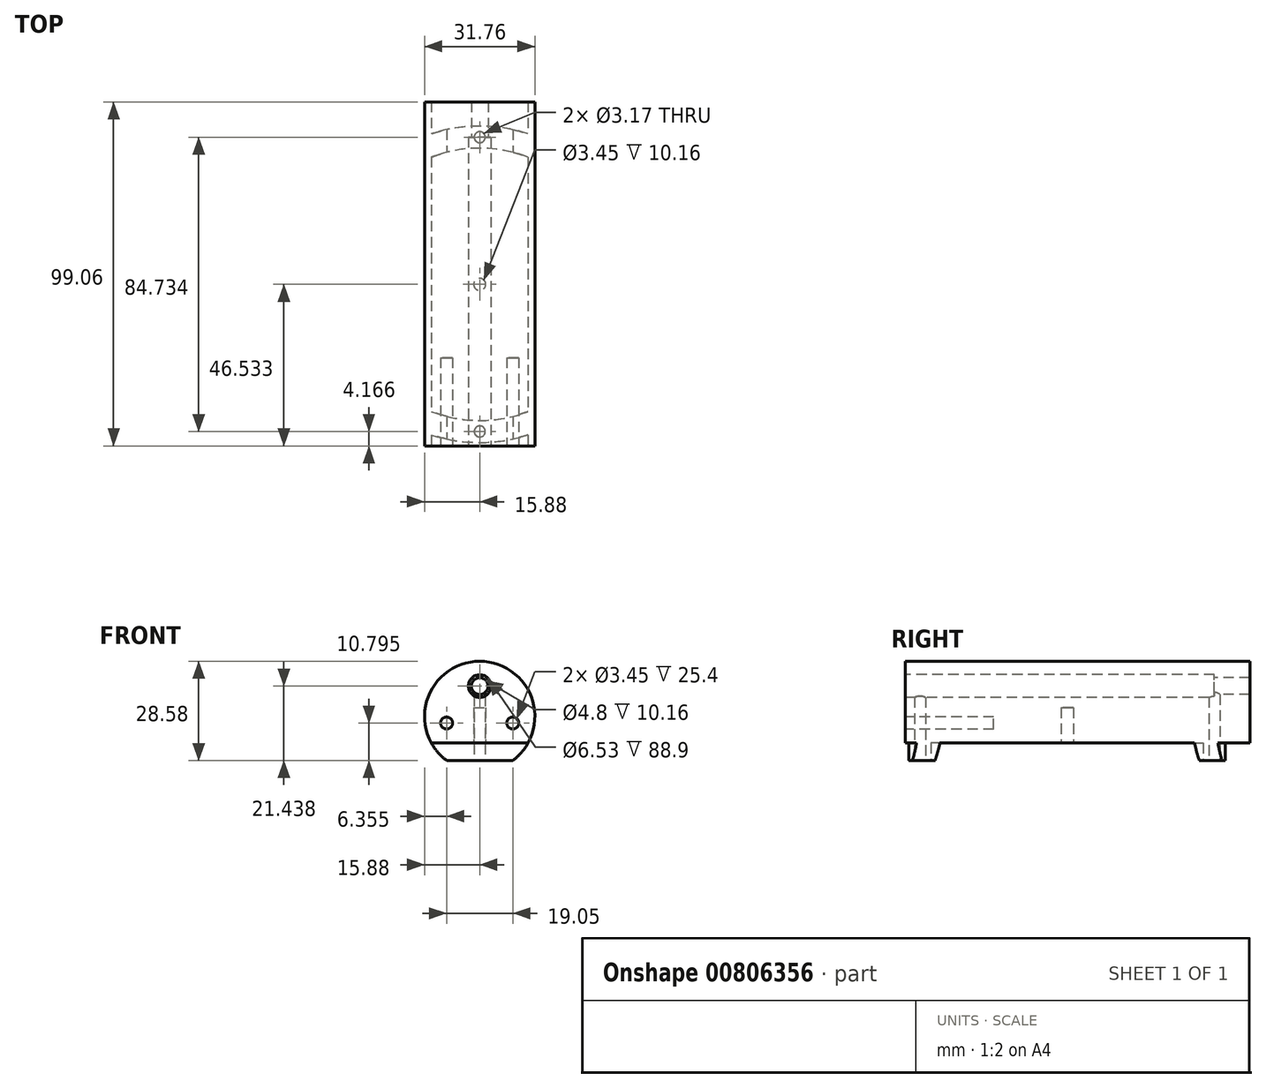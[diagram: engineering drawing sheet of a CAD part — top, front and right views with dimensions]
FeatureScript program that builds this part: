
annotation { "Feature Type Name" : "Feature", "Feature Type Description" : "" }
export const myFeature = defineFeature(function(context is Context, id is Id, definition is map)
    precondition{}
    {
        {
            var Q0;
            Q0=qCreatedBy(makeId("Front.planeOp"),FACE);
            var sketch = newSketch(context, id + "F0", { "sketchPlane" : qUnion([Q0])});
            skArc(sketch, "E0", {"start": v(9.52, -12.7) * mm, "mid": v(0, 15.88) * mm, "end": v(-9.53, -12.7) * mm});
            skLineSegment(sketch, "E1", {"start": v(-9.52, -12.7) * mm, "end": v(9.52, -12.7) * mm});
            skCircle(sketch, "E2", {"center": v(0, 8.74) * mm, "radius": 3.26 * mm});
            skLineSegment(sketch, "E3", {"start": v(-13.38, -1.9) * mm, "end": v(6.88, -1.9) * mm, "construction": true});
            skCircle(sketch, "E4", {"center": v(-9.52, -1.9) * mm, "radius": 1.73 * mm});
            skCircle(sketch, "E5", {"center": v(9.53, -1.9) * mm, "radius": 1.73 * mm});
            skCircle(sketch, "E6", {"center": v(0, 8.74) * mm, "radius": 2.4 * mm});
            skSolve(sketch);
        }
        {
            var Q0;
            Q0 = qSketchRegion(id + "F0", true);
            var Q1;
            Q1=makeQuery(id+"F0.imprint","IMPRINT",FACE,{"disambiguationData":[TD([[makeQuery(id+"F0.imprint","IMPRINT",EDGE,{"derivedFrom":sQuery(id+"F0.wireOp",EDGE,"E2")}),1.0]])]});
            var Q2;
            Q2=makeQuery(id+"F0.imprint","IMPRINT",FACE,{"disambiguationData":[TD([[makeQuery(id+"F0.imprint","IMPRINT",EDGE,{"derivedFrom":sQuery(id+"F0.wireOp",EDGE,"E4")}),1.0]])]});
            var Q3;
            Q3=makeQuery(id+"F0.imprint","IMPRINT",FACE,{"disambiguationData":[TD([[makeQuery(id+"F0.imprint","IMPRINT",EDGE,{"derivedFrom":sQuery(id+"F0.wireOp",EDGE,"E5")}),1.0]])]});
            extrude(context, id + "F1", {"entities" : qUnion([Q0, Q1, Q2, Q3]), "oppositeDirection" : true, "depth" : 99.06 * mm, "offsetDistance" : 25.4 * mm});
        }
        {
            var Q0;
            Q0=makeQuery(id+"F0.imprint","IMPRINT",FACE,{"disambiguationData":[TD([[makeQuery(id+"F0.imprint","IMPRINT",EDGE,{"derivedFrom":sQuery(id+"F0.wireOp",EDGE,"E2")}),1.0]])]});
            extrude(context, id + "F2", {"entities" : qUnion([Q0]), "operationType" : NewBodyOperationType.REMOVE, "endBound" : BoundingType.UP_TO_NEXT, "oppositeDirection" : true, "depth" : 25.4 * mm, "hasOffset" : true, "offsetDistance" : 10.16 * mm});
        }
        {
            var Q0;
            Q0=makeQuery(id+"F0.imprint","IMPRINT",FACE,{"disambiguationData":[TD([[makeQuery(id+"F0.imprint","IMPRINT",EDGE,{"derivedFrom":sQuery(id+"F0.wireOp",EDGE,"E4")}),1.0]])]});
            var Q1;
            Q1=makeQuery(id+"F0.imprint","IMPRINT",FACE,{"disambiguationData":[TD([[makeQuery(id+"F0.imprint","IMPRINT",EDGE,{"derivedFrom":sQuery(id+"F0.wireOp",EDGE,"E5")}),1.0]])]});
            extrude(context, id + "F3", {"entities" : qUnion([Q0, Q1]), "operationType" : NewBodyOperationType.REMOVE, "oppositeDirection" : true, "depth" : 25.4 * mm, "offsetDistance" : 25.4 * mm});
        }
        {
            var Q0;
            Q0=makeQuery(id+"F0.imprint","IMPRINT",FACE,{"disambiguationData":[TD([[makeQuery(id+"F0.imprint","IMPRINT",EDGE,{"derivedFrom":sQuery(id+"F0.wireOp",EDGE,"E6")}),1.0]])]});
            extrude(context, id + "F4", {"entities" : qUnion([Q0]), "operationType" : NewBodyOperationType.REMOVE, "endBound" : BoundingType.THROUGH_ALL, "oppositeDirection" : true, "depth" : 25.4 * mm, "offsetDistance" : 25.4 * mm});
        }
        {
            var Q0;
            Q0=makeQuery(id+"F1.opExtrude","SWEPT_FACE",FACE,{"disambiguationData":[OSD([sQuery(id+"F0.wireOp",EDGE,"E1")])]});
            var sketch = newSketch(context, id + "F5", { "sketchPlane" : qUnion([Q0])});
            skCircle(sketch, "E7", {"center": v(0, -46.53) * mm, "radius": 1.73 * mm});
            skCircle(sketch, "E8", {"center": v(0, -88.9) * mm, "radius": 1.59 * mm});
            skCircle(sketch, "E9", {"center": v(0, -4.17) * mm, "radius": 1.59 * mm});
            skArc(sketch, "E10.trimOffspring", {"start": v(9.53, -8.52) * mm, "mid": v(0, -7.34) * mm, "end": v(-9.53, -8.52) * mm});
            skArc(sketch, "E11.trimOffspring", {"start": v(9.52, -2) * mm, "mid": v(0, -1) * mm, "end": v(-9.53, -2) * mm});
            skLineSegment(sketch, "E12.bottom", {"start": v(-9.53, -99.06) * mm, "end": v(9.52, -99.06) * mm});
            skLineSegment(sketch, "E12.top", {"start": v(-9.53, 0) * mm, "end": v(9.52, 0) * mm});
            skLineSegment(sketch, "E13.bottom", {"start": v(9.52, -99.06) * mm, "end": v(19.26, -99.06) * mm});
            skLineSegment(sketch, "E13.top", {"start": v(9.52, 0) * mm, "end": v(19.26, 0) * mm});
            skLineSegment(sketch, "E13.right", {"start": v(19.26, -99.06) * mm, "end": v(19.26, 0) * mm});
            skLineSegment(sketch, "E14.bottom", {"start": v(-9.53, 0) * mm, "end": v(-24.1, 0) * mm});
            skLineSegment(sketch, "E14.top", {"start": v(-9.53, -99.06) * mm, "end": v(-24.1, -99.06) * mm});
            skLineSegment(sketch, "E14.right", {"start": v(-24.1, 0) * mm, "end": v(-24.1, -99.06) * mm});
            skArc(sketch, "E15.converted", {"start": v(19.26, -5.26) * mm, "mid": v(-2.76, -1.07) * mm, "end": v(-24.1, -7.9) * mm});
            skArc(sketch, "E16.converted", {"start": v(19.26, -12.4) * mm, "mid": v(-2.91, -7.45) * mm, "end": v(-24.1, -15.63) * mm});
            skArc(sketch, "E17.trimOffspring", {"start": v(-24.1, -77.43) * mm, "mid": v(-2.91, -85.62) * mm, "end": v(19.26, -80.67) * mm});
            skArc(sketch, "E18.trimOffspring", {"start": v(-24.1, -85.17) * mm, "mid": v(-2.76, -92) * mm, "end": v(19.26, -87.8) * mm});
            skSolve(sketch);
        }
        {
            var Q0;
            {var subQ0=sQuery(id+"F5.wireOp",EDGE,"E16.converted");var subQ1=sQuery(id+"F5.wireOp",EDGE,"E14.right");var subQ2=makeQuery(id+"F5.imprint","INTERSECT",VERTEX,{"derivedFrom":[subQ1,subQ0]});Q0=makeQuery(id+"F5.imprint","IMPRINT",FACE,{"disambiguationData":[TD([[makeQuery(id+"F5.imprint","IMPRINT",EDGE,{"disambiguationData":[TD([[subQ2,-1.0]])],"derivedFrom":subQ1}),1.0]])]});}
            var Q1;
            Q1=makeQuery(id+"F5.imprint","IMPRINT",FACE,{"disambiguationData":[TD([[makeQuery(id+"F5.imprint","IMPRINT",EDGE,{"derivedFrom":sQuery(id+"F5.wireOp",EDGE,"E7")}),-1.0]])]});
            var Q2;
            {var subQ0=sQuery(id+"F5.wireOp",EDGE,"E16.converted");var subQ1=sQuery(id+"F5.wireOp",EDGE,"E13.right");var subQ2=makeQuery(id+"F5.imprint","INTERSECT",VERTEX,{"derivedFrom":[subQ1,subQ0]});Q2=makeQuery(id+"F5.imprint","IMPRINT",FACE,{"disambiguationData":[TD([[makeQuery(id+"F5.imprint","IMPRINT",EDGE,{"disambiguationData":[TD([[subQ2,1.0]])],"derivedFrom":subQ1}),1.0]])]});}
            var Q3;
            {var subQ0=sQuery(id+"F5.wireOp",EDGE,"E13.bottom");Q3=makeQuery(id+"F5.imprint","IMPRINT",FACE,{"disambiguationData":[TD([[makeQuery(id+"F5.imprint","IMPRINT",EDGE,{"derivedFrom":subQ0}),1.0]])]});}
            var Q4;
            {var subQ0=sQuery(id+"F5.wireOp",EDGE,"E12.bottom");Q4=makeQuery(id+"F5.imprint","IMPRINT",FACE,{"disambiguationData":[TD([[makeQuery(id+"F5.imprint","IMPRINT",EDGE,{"derivedFrom":subQ0}),1.0]])]});}
            var Q5;
            {var subQ0=sQuery(id+"F5.wireOp",EDGE,"E14.top");Q5=makeQuery(id+"F5.imprint","IMPRINT",FACE,{"disambiguationData":[TD([[makeQuery(id+"F5.imprint","IMPRINT",EDGE,{"derivedFrom":subQ0}),-1.0]])]});}
            var Q6;
            {var subQ0=sQuery(id+"F5.wireOp",EDGE,"E13.top");Q6=makeQuery(id+"F5.imprint","IMPRINT",FACE,{"disambiguationData":[TD([[makeQuery(id+"F5.imprint","IMPRINT",EDGE,{"derivedFrom":subQ0}),-1.0]])]});}
            var Q7;
            {var subQ0=sQuery(id+"F5.wireOp",EDGE,"E12.top");Q7=makeQuery(id+"F5.imprint","IMPRINT",FACE,{"disambiguationData":[TD([[makeQuery(id+"F5.imprint","IMPRINT",EDGE,{"derivedFrom":subQ0}),-1.0]])]});}
            var Q8;
            {var subQ0=sQuery(id+"F5.wireOp",EDGE,"E14.bottom");Q8=makeQuery(id+"F5.imprint","IMPRINT",FACE,{"disambiguationData":[TD([[makeQuery(id+"F5.imprint","IMPRINT",EDGE,{"derivedFrom":subQ0}),1.0]])]});}
            extrude(context, id + "F6", {"entities" : qUnion([Q0, Q1, Q2, Q3, Q4, Q5, Q6, Q7, Q8]), "operationType" : NewBodyOperationType.REMOVE, "oppositeDirection" : true, "depth" : 5.08 * mm, "offsetDistance" : 25.4 * mm});
        }
        {
            var Q0;
            Q0=makeQuery(id+"F5.imprint","IMPRINT",FACE,{"disambiguationData":[TD([[makeQuery(id+"F5.imprint","IMPRINT",EDGE,{"derivedFrom":sQuery(id+"F5.wireOp",EDGE,"E7")}),1.0]])]});
            extrude(context, id + "F7", {"entities" : qUnion([Q0]), "operationType" : NewBodyOperationType.REMOVE, "oppositeDirection" : true, "depth" : 15.24 * mm, "offsetDistance" : 25.4 * mm});
        }
        {
            var Q0;
            Q0=makeQuery(id+"F5.imprint","IMPRINT",FACE,{"disambiguationData":[TD([[makeQuery(id+"F5.imprint","IMPRINT",EDGE,{"derivedFrom":sQuery(id+"F5.wireOp",EDGE,"E8")}),1.0]])]});
            var Q1;
            Q1=makeQuery(id+"F5.imprint","IMPRINT",FACE,{"disambiguationData":[TD([[makeQuery(id+"F5.imprint","IMPRINT",EDGE,{"derivedFrom":sQuery(id+"F5.wireOp",EDGE,"E9")}),1.0]])]});
            extrude(context, id + "F8", {"entities" : qUnion([Q0, Q1]), "operationType" : NewBodyOperationType.REMOVE, "endBound" : BoundingType.UP_TO_NEXT, "oppositeDirection" : true, "depth" : 25.4 * mm, "offsetDistance" : 25.4 * mm});
        }
    });
